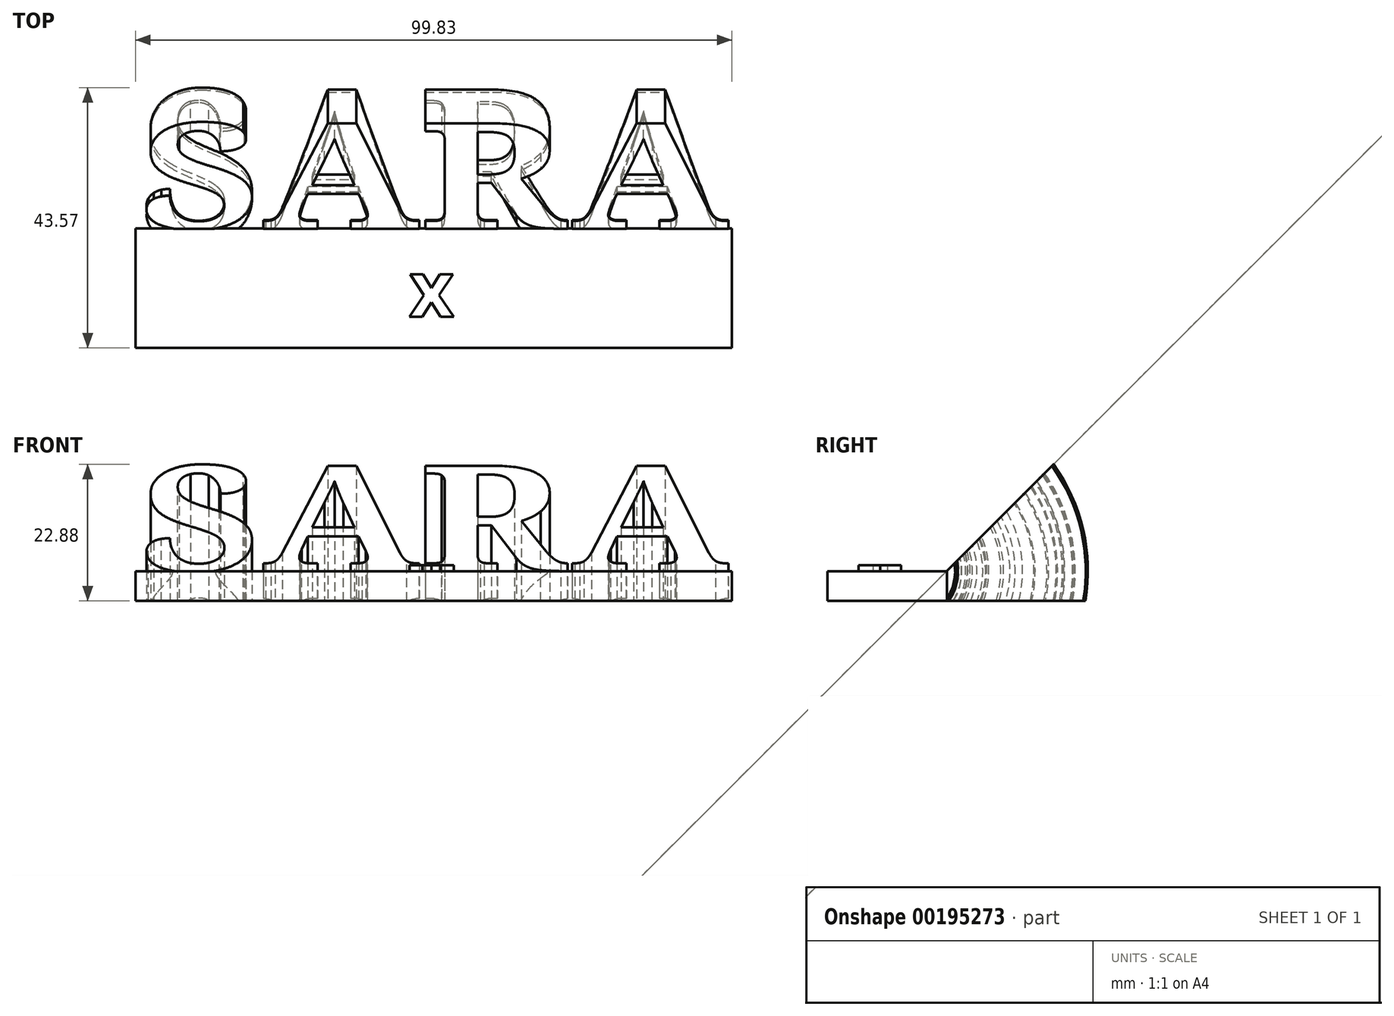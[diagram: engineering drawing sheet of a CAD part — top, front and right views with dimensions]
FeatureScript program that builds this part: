
annotation { "Feature Type Name" : "Feature", "Feature Type Description" : "" }
export const myFeature = defineFeature(function(context is Context, id is Id, definition is map)
    precondition{}
    {
        {
            var Q0;
            Q0=qCreatedBy(makeId("Top.planeOp"),FACE);
            var sketch = newSketch(context, id + "F0", { "sketchPlane" : qUnion([Q0])});
            skText(sketch, "E0", { "text": "SARA", "fontName": "NotoSerif-Bold.ttf"});
            const initialGuessF0  = {"E0": [-0.05, -0.01761, 1, 0, 0.02514]};
            skSetInitialGuess(sketch, initialGuessF0);
            skSolve(sketch);
        }
        {
            var Q0;
            Q0=makeQuery(id+"F0.imprint","IMPRINT",FACE,{"disambiguationData":[TD([[makeQuery(id+"F0.imprint","IMPRINT",EDGE,{"derivedFrom":sQuery(id+"F0.wireOp",EDGE,"E0.sketch_text.stroke-28")}),-1.0]])]});
            cPlane(context, id + "F1", {"entities" : qUnion([Q0]), "cplaneType" : CPlaneType.OFFSET, "offset" : 5 * mm, "width" : 152.4 * mm, "height" : 152.4 * mm});
        }
        {
            var Q0;
            Q0=qCreatedBy(id+"F1.planeOp",FACE);
            var sketch = newSketch(context, id + "F2", { "sketchPlane" : qUnion([Q0])});
            skLineSegment(sketch, "E1", {"start": v(-51.29, -22.61) * mm, "end": v(46.8, -22.61) * mm});
            skSolve(sketch);
        }
        {
            var Q0;
            Q0=makeQuery(id+"F0.imprint","IMPRINT",FACE,{"disambiguationData":[TD([[makeQuery(id+"F0.imprint","IMPRINT",EDGE,{"derivedFrom":sQuery(id+"F0.wireOp",EDGE,"E0.sketch_text.stroke-0")}),-1.0]])]});
            var Q1;
            Q1=makeQuery(id+"F0.imprint","IMPRINT",FACE,{"disambiguationData":[TD([[makeQuery(id+"F0.imprint","IMPRINT",EDGE,{"derivedFrom":sQuery(id+"F0.wireOp",EDGE,"E0.sketch_text.stroke-28")}),-1.0]])]});
            var Q2;
            Q2=makeQuery(id+"F0.imprint","IMPRINT",FACE,{"disambiguationData":[TD([[makeQuery(id+"F0.imprint","IMPRINT",EDGE,{"derivedFrom":sQuery(id+"F0.wireOp",EDGE,"E0.sketch_text.stroke-56")}),-1.0]])]});
            var Q3;
            Q3=makeQuery(id+"F0.imprint","IMPRINT",FACE,{"disambiguationData":[TD([[makeQuery(id+"F0.imprint","IMPRINT",EDGE,{"derivedFrom":sQuery(id+"F0.wireOp",EDGE,"E0.sketch_text.stroke-112")}),-1.0]])]});
            var Q4;
            Q4=makeQuery(id+"F0.imprint","IMPRINT",FACE,{"disambiguationData":[TD([[makeQuery(id+"F0.imprint","IMPRINT",EDGE,{"derivedFrom":sQuery(id+"F0.wireOp",EDGE,"E0.sketch_text.stroke-156")}),-1.0]])]});
            var Q5;
            Q5=sQuery(id+"F2.wireOp",EDGE,"E1");
            revolve(context, id + "F3", {"entities" : qUnion([Q0, Q1, Q2, Q3, Q4]), "axis" : qUnion([Q5]), "revolveType" : RevolveType.ONE_DIRECTION, "angle" : 45 * degree});
        }
        {
            var Q0;
            Q0=qCreatedBy(makeId("Top.planeOp"),FACE);
            var sketch = newSketch(context, id + "F4", { "sketchPlane" : qUnion([Q0])});
            skLineSegment(sketch, "E2.bottom", {"start": v(-50.77, -15.5) * mm, "end": v(49.06, -15.5) * mm});
            skLineSegment(sketch, "E2.top", {"start": v(-50.77, -35.5) * mm, "end": v(49.06, -35.5) * mm});
            skLineSegment(sketch, "E2.left", {"start": v(-50.77, -15.5) * mm, "end": v(-50.77, -35.5) * mm});
            skLineSegment(sketch, "E2.right", {"start": v(49.06, -15.5) * mm, "end": v(49.06, -35.5) * mm});
            skSolve(sketch);
        }
        {
            var Q0;
            Q0=makeQuery(id+"F4.imprint","IMPRINT",FACE,{"disambiguationData":[TD([[makeQuery(id+"F4.imprint","IMPRINT",EDGE,{"derivedFrom":sQuery(id+"F4.wireOp",EDGE,"E2.bottom")}),-1.0]])]});
            extrude(context, id + "F5", {"entities" : qUnion([Q0]), "operationType" : NewBodyOperationType.ADD, "depth" : 5 * mm});
        }
        {
            var Q0;
            Q0=makeQuery(id+"F5.opExtrude","CAP_FACE",FACE,{"disambiguationData":[OSD([sQuery(id+"F4.wireOp",EDGE,"E2.bottom"),sQuery(id+"F4.wireOp",EDGE,"E2.top"),sQuery(id+"F4.wireOp",EDGE,"E2.left"),sQuery(id+"F4.wireOp",EDGE,"E2.right")])],"isStart":false});
            var sketch = newSketch(context, id + "F6", { "sketchPlane" : qUnion([Q0])});
            skText(sketch, "E3", { "text": "x", "fontName": "OpenSans-Bold.ttf"});
            skLineSegment(sketch, "E4", {"start": v(-0.85, -35.5) * mm, "end": v(-0.85, -6.28) * mm, "construction": true});
            const initialGuessF6  = {"E3": [-0.00502, -0.0303, 1, 0, 0.00941]};
            skSetInitialGuess(sketch, initialGuessF6);
            skSolve(sketch);
        }
        {
            var Q0;
            Q0=qSketchRegion(id+"F6",true);
            extrude(context, id + "F7", {"entities" : qUnion([Q0]), "operationType" : NewBodyOperationType.ADD, "depth" : 1 * mm});
        }
    });
